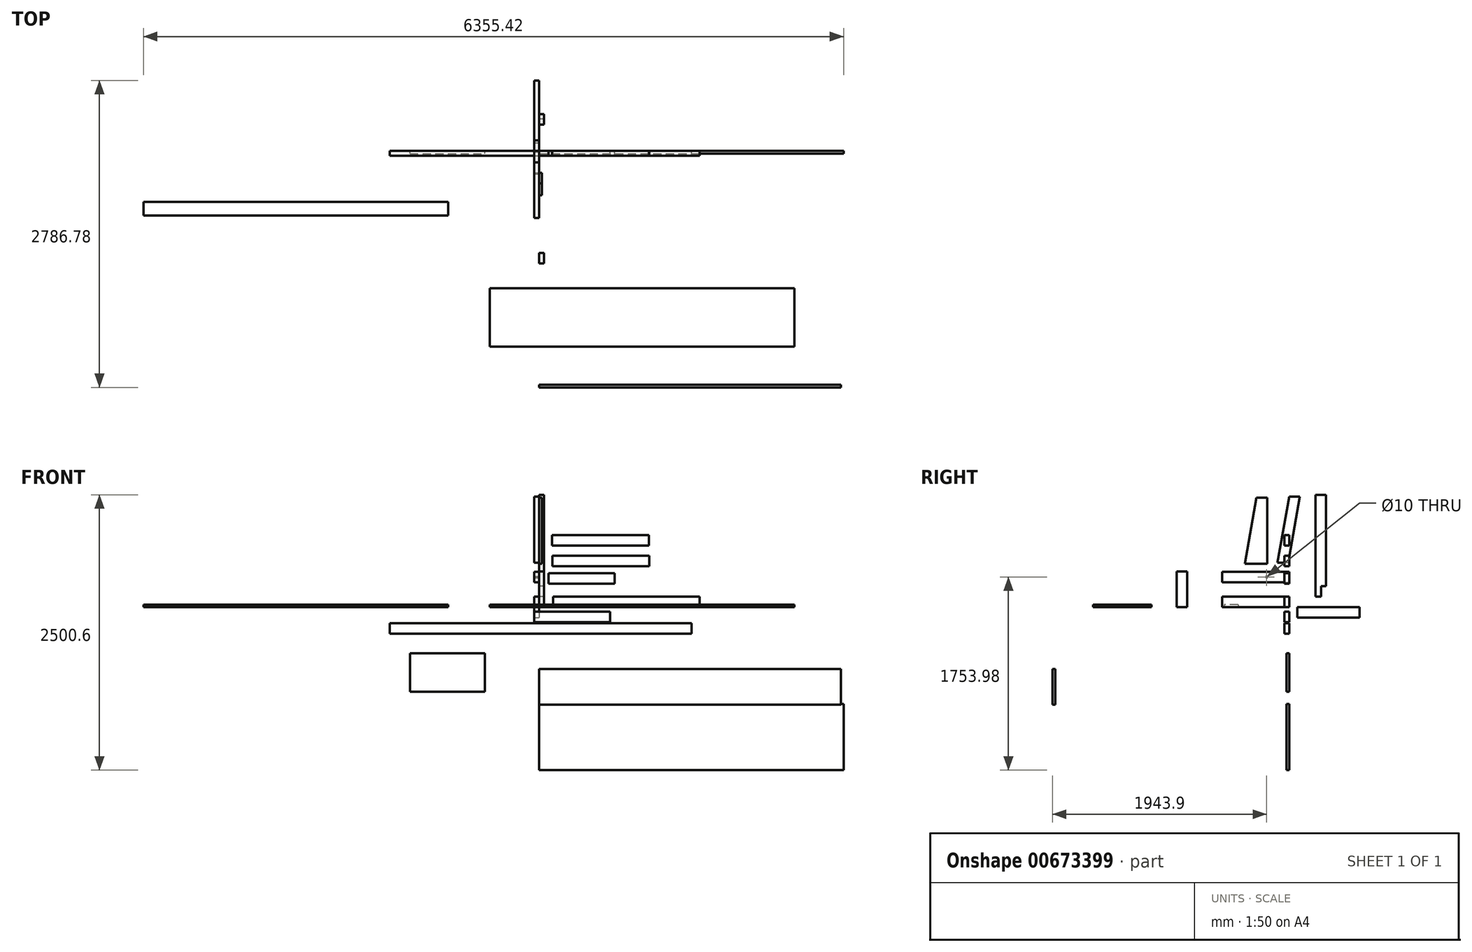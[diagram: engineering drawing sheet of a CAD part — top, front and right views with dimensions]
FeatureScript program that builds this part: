
annotation { "Feature Type Name" : "Feature", "Feature Type Description" : "" }
export const myFeature = defineFeature(function(context is Context, id is Id, definition is map)
    precondition{}
    {
        {
            var Q0;
            Q0=qCreatedBy(makeId("Right.planeOp"),FACE);
            var sketch = newSketch(context, id + "F0", { "sketchPlane" : qUnion([Q0])});
            skLineSegment(sketch, "E0", {"start": v(0, 1003.33) * mm, "end": v(-106.38, 403.33) * mm});
            skLineSegment(sketch, "E1", {"start": v(96.47, 1003.24) * mm, "end": v(-9.92, 403.24) * mm});
            skLineSegment(sketch, "E2", {"start": v(0, 1003.33) * mm, "end": v(96.47, 1003.24) * mm});
            skLineSegment(sketch, "E3", {"start": v(-9.92, 403.24) * mm, "end": v(-106.38, 403.33) * mm});
            skSolve(sketch);
        }
        {
            var Q0;
            Q0=makeQuery(id+"F0.imprint","IMPRINT",FACE,{"disambiguationData":[TD([[makeQuery(id+"F0.imprint","IMPRINT",EDGE,{"derivedFrom":sQuery(id+"F0.wireOp",EDGE,"E0")}),1.0]])]});
            extrude(context, id + "F1", {"entities" : qUnion([Q0]), "oppositeDirection" : true, "depth" : 45 * mm, "offsetDistance" : 25 * mm});
        }
        {
            var Q0;
            Q0=qCreatedBy(makeId("Right.planeOp"),FACE);
            var sketch = newSketch(context, id + "F2", { "sketchPlane" : qUnion([Q0])});
            skLineSegment(sketch, "E4.bottom", {"start": v(-610, 321.93) * mm, "end": v(0, 321.93) * mm});
            skLineSegment(sketch, "E4.top", {"start": v(-610, 226.93) * mm, "end": v(0, 226.93) * mm});
            skLineSegment(sketch, "E4.left", {"start": v(-610, 321.93) * mm, "end": v(-610, 226.93) * mm});
            skLineSegment(sketch, "E4.right", {"start": v(0, 321.93) * mm, "end": v(0, 226.93) * mm});
            skPoint(sketch, "E5.positionSnap0", {"position": v(0, 274.43) * mm});
            skCircle(sketch, "E6", {"center": v(-205, 274.43) * mm, "radius": 5 * mm});
            skSolve(sketch);
        }
        {
            var Q0;
            Q0 = qSketchRegion(id + "F2", true);
            extrude(context, id + "F3", {"entities" : qUnion([Q0]), "oppositeDirection" : true, "depth" : 45 * mm, "offsetDistance" : 25 * mm});
        }
        {
            var Q0;
            Q0=qCreatedBy(makeId("Right.planeOp"),FACE);
            var sketch = newSketch(context, id + "F4", { "sketchPlane" : qUnion([Q0])});
            skLineSegment(sketch, "E7.bottom", {"start": v(334, 1021.05) * mm, "end": v(239, 1021.05) * mm});
            skLineSegment(sketch, "E7.top", {"start": v(334, 96.05) * mm, "end": v(239, 96.05) * mm});
            skLineSegment(sketch, "E7.left", {"start": v(334, 1021.05) * mm, "end": v(334, 96.05) * mm});
            skLineSegment(sketch, "E7.right", {"start": v(239, 1021.05) * mm, "end": v(239, 96.05) * mm});
            skLineSegment(sketch, "E8.bottom", {"start": v(334, 96.05) * mm, "end": v(289, 96.05) * mm});
            skLineSegment(sketch, "E8.top", {"start": v(334, 191.05) * mm, "end": v(289, 191.05) * mm});
            skLineSegment(sketch, "E8.left", {"start": v(334, 96.05) * mm, "end": v(334, 191.05) * mm});
            skLineSegment(sketch, "E8.right", {"start": v(289, 96.05) * mm, "end": v(289, 191.05) * mm});
            skSolve(sketch);
        }
        {
            var Q0;
            Q0=makeQuery(id+"F4.imprint","IMPRINT",FACE,{"disambiguationData":[TD([[makeQuery(id+"F4.imprint","IMPRINT",EDGE,{"derivedFrom":sQuery(id+"F4.wireOp",EDGE,"E7.bottom")}),1.0]])]});
            extrude(context, id + "F5", {"entities" : qUnion([Q0]), "depth" : 45 * mm, "offsetDistance" : 25 * mm});
        }
        {
            var Q0;
            Q0=qCreatedBy(makeId("Right.planeOp"),FACE);
            var sketch = newSketch(context, id + "F6", { "sketchPlane" : qUnion([Q0])});
            skLineSegment(sketch, "E9.bottom", {"start": v(0, 0) * mm, "end": v(-610, 0) * mm});
            skLineSegment(sketch, "E9.top", {"start": v(0, 95) * mm, "end": v(-610, 95) * mm});
            skLineSegment(sketch, "E9.left", {"start": v(0, 0) * mm, "end": v(0, 95) * mm});
            skLineSegment(sketch, "E9.right", {"start": v(-610, 0) * mm, "end": v(-610, 95) * mm});
            skSolve(sketch);
        }
        {
            var Q0;
            Q0=makeQuery(id+"F6.imprint","IMPRINT",FACE,{"disambiguationData":[TD([[makeQuery(id+"F6.imprint","IMPRINT",EDGE,{"derivedFrom":sQuery(id+"F6.wireOp",EDGE,"E9.bottom")}),-1.0]])]});
            extrude(context, id + "F7", {"entities" : qUnion([Q0]), "oppositeDirection" : true, "depth" : 45 * mm, "offsetDistance" : 25 * mm});
        }
        {
            var Q0;
            Q0=qCreatedBy(makeId("Right.planeOp"),FACE);
            var sketch = newSketch(context, id + "F8", { "sketchPlane" : qUnion([Q0])});
            skLineSegment(sketch, "E10.bottom", {"start": v(-1022.82, 325) * mm, "end": v(-927.82, 325) * mm});
            skLineSegment(sketch, "E10.top", {"start": v(-1022.82, 0) * mm, "end": v(-927.82, 0) * mm});
            skLineSegment(sketch, "E10.left", {"start": v(-1022.82, 325) * mm, "end": v(-1022.82, 0) * mm});
            skLineSegment(sketch, "E10.right", {"start": v(-927.82, 325) * mm, "end": v(-927.82, 0) * mm});
            skSolve(sketch);
        }
        {
            var Q0;
            Q0=makeQuery(id+"F8.imprint","IMPRINT",FACE,{"disambiguationData":[TD([[makeQuery(id+"F8.imprint","IMPRINT",EDGE,{"derivedFrom":sQuery(id+"F8.wireOp",EDGE,"E10.bottom")}),-1.0]])]});
            extrude(context, id + "F9", {"entities" : qUnion([Q0]), "depth" : 45 * mm, "offsetDistance" : 25 * mm});
        }
        {
            var Q0;
            Q0=qCreatedBy(makeId("Front.planeOp"),FACE);
            var sketch = newSketch(context, id + "F10", { "sketchPlane" : qUnion([Q0])});
            skLineSegment(sketch, "E11.bottom", {"start": v(126.86, 0) * mm, "end": v(1456.86, 0) * mm});
            skLineSegment(sketch, "E11.top", {"start": v(126.86, 95) * mm, "end": v(1456.86, 95) * mm});
            skLineSegment(sketch, "E11.left", {"start": v(126.86, 0) * mm, "end": v(126.86, 95) * mm});
            skLineSegment(sketch, "E11.right", {"start": v(1456.86, 0) * mm, "end": v(1456.86, 95) * mm});
            skSolve(sketch);
        }
        {
            var Q0;
            Q0=makeQuery(id+"F10.imprint","IMPRINT",FACE,{"disambiguationData":[TD([[makeQuery(id+"F10.imprint","IMPRINT",EDGE,{"derivedFrom":sQuery(id+"F10.wireOp",EDGE,"E11.bottom")}),1.0]])]});
            extrude(context, id + "F11", {"entities" : qUnion([Q0]), "depth" : 45 * mm, "offsetDistance" : 25 * mm});
        }
        {
            var Q0;
            Q0=qCreatedBy(makeId("Right.planeOp"),FACE);
            var sketch = newSketch(context, id + "F12", { "sketchPlane" : qUnion([Q0])});
            skLineSegment(sketch, "E12.bottom", {"start": v(72.88, 0) * mm, "end": v(637.88, 0) * mm});
            skLineSegment(sketch, "E12.top", {"start": v(72.88, -95) * mm, "end": v(637.88, -95) * mm});
            skLineSegment(sketch, "E12.left", {"start": v(72.88, 0) * mm, "end": v(72.88, -95) * mm});
            skLineSegment(sketch, "E12.right", {"start": v(637.88, 0) * mm, "end": v(637.88, -95) * mm});
            skSolve(sketch);
        }
        {
            var Q0;
            Q0=makeQuery(id+"F12.imprint","IMPRINT",FACE,{"disambiguationData":[TD([[makeQuery(id+"F12.imprint","IMPRINT",EDGE,{"derivedFrom":sQuery(id+"F12.wireOp",EDGE,"E12.bottom")}),-1.0]])]});
            extrude(context, id + "F13", {"entities" : qUnion([Q0]), "oppositeDirection" : true, "depth" : 45 * mm, "offsetDistance" : 25 * mm});
        }
        {
            var Q0;
            Q0=qCreatedBy(makeId("Front.planeOp"),FACE);
            var sketch = newSketch(context, id + "F14", { "sketchPlane" : qUnion([Q0])});
            skLineSegment(sketch, "E13.bottom", {"start": v(87.25, 309.2) * mm, "end": v(684.75, 309.2) * mm});
            skLineSegment(sketch, "E13.top", {"start": v(87.25, 214.2) * mm, "end": v(684.75, 214.2) * mm});
            skLineSegment(sketch, "E13.left", {"start": v(87.25, 309.2) * mm, "end": v(87.25, 214.2) * mm});
            skLineSegment(sketch, "E13.right", {"start": v(684.75, 309.2) * mm, "end": v(684.75, 214.2) * mm});
            skSolve(sketch);
        }
        {
            var Q0;
            Q0 = qSketchRegion(id + "F14", true);
            extrude(context, id + "F15", {"entities" : qUnion([Q0]), "depth" : 45 * mm, "offsetDistance" : 25 * mm});
        }
        {
            var Q0;
            Q0=qCreatedBy(makeId("Front.planeOp"),FACE);
            var sketch = newSketch(context, id + "F16", { "sketchPlane" : qUnion([Q0])});
            skLineSegment(sketch, "E14.bottom", {"start": v(-43.15, -41.16) * mm, "end": v(644.35, -41.16) * mm});
            skLineSegment(sketch, "E14.top", {"start": v(-43.15, -136.16) * mm, "end": v(644.35, -136.16) * mm});
            skLineSegment(sketch, "E14.left", {"start": v(-43.15, -41.16) * mm, "end": v(-43.15, -136.16) * mm});
            skLineSegment(sketch, "E14.right", {"start": v(644.35, -41.16) * mm, "end": v(644.35, -136.16) * mm});
            skSolve(sketch);
        }
        {
            var Q0;
            Q0 = qSketchRegion(id + "F16", true);
            extrude(context, id + "F17", {"entities" : qUnion([Q0]), "depth" : 45 * mm, "offsetDistance" : 25 * mm});
        }
        {
            var Q0;
            Q0=qCreatedBy(makeId("Front.planeOp"),FACE);
            var sketch = newSketch(context, id + "F18", { "sketchPlane" : qUnion([Q0])});
            skLineSegment(sketch, "E15.bottom", {"start": v(121.17, 466.86) * mm, "end": v(1001.17, 466.86) * mm});
            skLineSegment(sketch, "E15.top", {"start": v(121.17, 371.86) * mm, "end": v(1001.17, 371.86) * mm});
            skLineSegment(sketch, "E15.left", {"start": v(121.17, 466.86) * mm, "end": v(121.17, 371.86) * mm});
            skLineSegment(sketch, "E15.right", {"start": v(1001.17, 466.86) * mm, "end": v(1001.17, 371.86) * mm});
            skSolve(sketch);
        }
        {
            var Q0;
            Q0=makeQuery(id+"F18.imprint","IMPRINT",FACE,{"disambiguationData":[TD([[makeQuery(id+"F18.imprint","IMPRINT",EDGE,{"derivedFrom":sQuery(id+"F18.wireOp",EDGE,"E15.bottom")}),-1.0]])]});
            extrude(context, id + "F19", {"entities" : qUnion([Q0]), "depth" : 45 * mm, "offsetDistance" : 25 * mm});
        }
        {
            var Q0;
            Q0=qCreatedBy(makeId("Front.planeOp"),FACE);
            var sketch = newSketch(context, id + "F20", { "sketchPlane" : qUnion([Q0])});
            skLineSegment(sketch, "E16.bottom", {"start": v(116.72, 654.45) * mm, "end": v(996.72, 654.45) * mm});
            skLineSegment(sketch, "E16.top", {"start": v(116.72, 559.45) * mm, "end": v(996.72, 559.45) * mm});
            skLineSegment(sketch, "E16.left", {"start": v(116.72, 654.45) * mm, "end": v(116.72, 559.45) * mm});
            skLineSegment(sketch, "E16.right", {"start": v(996.72, 654.45) * mm, "end": v(996.72, 559.45) * mm});
            skSolve(sketch);
        }
        {
            var Q0;
            Q0=makeQuery(id+"F20.imprint","IMPRINT",FACE,{"disambiguationData":[TD([[makeQuery(id+"F20.imprint","IMPRINT",EDGE,{"derivedFrom":sQuery(id+"F20.wireOp",EDGE,"E16.bottom")}),-1.0]])]});
            extrude(context, id + "F21", {"entities" : qUnion([Q0]), "depth" : 45 * mm, "offsetDistance" : 25 * mm});
        }
        {
            var Q0;
            Q0=qCreatedBy(makeId("Front.planeOp"),FACE);
            var sketch = newSketch(context, id + "F22", { "sketchPlane" : qUnion([Q0])});
            skLineSegment(sketch, "E17.bottom", {"start": v(-1356.74, -144.71) * mm, "end": v(1383.26, -144.71) * mm});
            skLineSegment(sketch, "E17.top", {"start": v(-1356.74, -239.71) * mm, "end": v(1383.26, -239.71) * mm});
            skLineSegment(sketch, "E17.left", {"start": v(-1356.74, -144.71) * mm, "end": v(-1356.74, -239.71) * mm});
            skLineSegment(sketch, "E17.right", {"start": v(1383.26, -144.71) * mm, "end": v(1383.26, -239.71) * mm});
            skSolve(sketch);
        }
        {
            var Q0;
            Q0=makeQuery(id+"F22.imprint","IMPRINT",FACE,{"disambiguationData":[TD([[makeQuery(id+"F22.imprint","IMPRINT",EDGE,{"derivedFrom":sQuery(id+"F22.wireOp",EDGE,"E17.bottom")}),-1.0]])]});
            extrude(context, id + "F23", {"entities" : qUnion([Q0]), "depth" : 45 * mm, "offsetDistance" : 25 * mm});
        }
        {
            var Q0;
            Q0=qCreatedBy(makeId("Front.planeOp"),FACE);
            var sketch = newSketch(context, id + "F24", { "sketchPlane" : qUnion([Q0])});
            skLineSegment(sketch, "E18.bottom", {"start": v(-1172.12, -416.8) * mm, "end": v(-492.12, -416.8) * mm});
            skLineSegment(sketch, "E18.top", {"start": v(-1172.12, -766.8) * mm, "end": v(-492.12, -766.8) * mm});
            skLineSegment(sketch, "E18.left", {"start": v(-1172.12, -416.8) * mm, "end": v(-1172.12, -766.8) * mm});
            skLineSegment(sketch, "E18.right", {"start": v(-492.12, -416.8) * mm, "end": v(-492.12, -766.8) * mm});
            skSolve(sketch);
        }
        {
            var Q0;
            Q0=makeQuery(id+"F24.imprint","IMPRINT",FACE,{"disambiguationData":[TD([[makeQuery(id+"F24.imprint","IMPRINT",EDGE,{"derivedFrom":sQuery(id+"F24.wireOp",EDGE,"E18.bottom")}),-1.0]])]});
            extrude(context, id + "F25", {"entities" : qUnion([Q0]), "depth" : 25 * mm, "offsetDistance" : 25 * mm});
        }
        {
            var Q0;
            Q0=qCreatedBy(makeId("Right.planeOp"),FACE);
            var sketch = newSketch(context, id + "F26", { "sketchPlane" : qUnion([Q0])});
            skLineSegment(sketch, "E19.bottom", {"start": v(616.1, -559.45) * mm, "end": v(-2123.9, -559.45) * mm});
            skLineSegment(sketch, "E19.top", {"start": v(616.1, -884.45) * mm, "end": v(-2123.9, -884.45) * mm});
            skLineSegment(sketch, "E19.left", {"start": v(616.1, -559.45) * mm, "end": v(616.1, -884.45) * mm});
            skLineSegment(sketch, "E19.right", {"start": v(-2123.9, -559.45) * mm, "end": v(-2123.9, -884.45) * mm});
            skSolve(sketch);
        }
        {
            var Q0;
            Q0=makeQuery(id+"F26.imprint","IMPRINT",FACE,{"disambiguationData":[TD([[makeQuery(id+"F26.imprint","IMPRINT",EDGE,{"derivedFrom":sQuery(id+"F26.wireOp",EDGE,"E19.bottom")}),1.0]])]});
            extrude(context, id + "F27", {"entities" : qUnion([Q0]), "depth" : 25 * mm, "offsetDistance" : 25 * mm});
        }
        {
            var Q0;
            Q0=makeQuery(id+"F27.opExtrude","SWEPT_BODY",BODY,{"disambiguationData":[OSD([sQuery(id+"F26.wireOp",EDGE,"E19.bottom"),sQuery(id+"F26.wireOp",EDGE,"E19.top"),sQuery(id+"F26.wireOp",EDGE,"E19.left"),sQuery(id+"F26.wireOp",EDGE,"E19.right")])]});
            var Q1;
            Q1=makeQuery(id+"F27.opExtrude","CAP_EDGE",EDGE,{"disambiguationData":[OSD([sQuery(id+"F26.wireOp",EDGE,"E19.right")])],"isStart":true});
            transform(context, id + "F28", {"entities" : qUnion([Q0]), "transformType" : TransformType.ROTATION, "transformAxis" : qUnion([Q1]), "angle" : 90 * degree, "makeCopy" : false});
        }
        {
            var Q0;
            Q0=qCreatedBy(makeId("Right.planeOp"),FACE);
            var sketch = newSketch(context, id + "F29", { "sketchPlane" : qUnion([Q0])});
            skLineSegment(sketch, "E20", {"start": v(-200.62, 995.97) * mm, "end": v(-297.09, 995.97) * mm});
            skLineSegment(sketch, "E21", {"start": v(-297.09, 995.97) * mm, "end": v(-402.89, 395.97) * mm});
            skLineSegment(sketch, "E22", {"start": v(-402.89, 395.97) * mm, "end": v(-200.62, 395.97) * mm});
            skLineSegment(sketch, "E23", {"start": v(-200.62, 395.97) * mm, "end": v(-200.62, 995.97) * mm});
            skSolve(sketch);
        }
        {
            var Q0;
            Q0=makeQuery(id+"F29.imprint","IMPRINT",FACE,{"disambiguationData":[TD([[makeQuery(id+"F29.imprint","IMPRINT",EDGE,{"derivedFrom":sQuery(id+"F29.wireOp",EDGE,"E20")}),1.0]])]});
            extrude(context, id + "F30", {"entities" : qUnion([Q0]), "depth" : 25 * mm, "offsetDistance" : 25 * mm});
        }
        {
            var Q0;
            Q0=qCreatedBy(makeId("Top.planeOp"),FACE);
            var sketch = newSketch(context, id + "F31", { "sketchPlane" : qUnion([Q0])});
            skLineSegment(sketch, "E24.bottom", {"start": v(-445.96, -1248.84) * mm, "end": v(2319.04, -1248.84) * mm});
            skLineSegment(sketch, "E24.top", {"start": v(-445.96, -1778.84) * mm, "end": v(2319.04, -1778.84) * mm});
            skLineSegment(sketch, "E24.left", {"start": v(-445.96, -1248.84) * mm, "end": v(-445.96, -1778.84) * mm});
            skLineSegment(sketch, "E24.right", {"start": v(2319.04, -1248.84) * mm, "end": v(2319.04, -1778.84) * mm});
            skSolve(sketch);
        }
        {
            var Q0;
            Q0 = qSketchRegion(id + "F31", true);
            extrude(context, id + "F32", {"entities" : qUnion([Q0]), "depth" : 25 * mm, "offsetDistance" : 25 * mm});
        }
        {
            var Q0;
            Q0=qCreatedBy(makeId("Front.planeOp"),FACE);
            var sketch = newSketch(context, id + "F33", { "sketchPlane" : qUnion([Q0])});
            skLineSegment(sketch, "E25.bottom", {"start": v(0, -879.55) * mm, "end": v(2765, -879.55) * mm});
            skLineSegment(sketch, "E25.top", {"start": v(0, -1479.55) * mm, "end": v(2765, -1479.55) * mm});
            skLineSegment(sketch, "E25.left", {"start": v(0, -879.55) * mm, "end": v(0, -1479.55) * mm});
            skLineSegment(sketch, "E25.right", {"start": v(2765, -879.55) * mm, "end": v(2765, -1479.55) * mm});
            skSolve(sketch);
        }
        {
            var Q0;
            Q0 = qSketchRegion(id + "F33", true);
            extrude(context, id + "F34", {"entities" : qUnion([Q0]), "depth" : 25 * mm, "offsetDistance" : 25 * mm});
        }
        {
            var Q0;
            Q0=qCreatedBy(makeId("Top.planeOp"),FACE);
            var sketch = newSketch(context, id + "F35", { "sketchPlane" : qUnion([Q0])});
            skLineSegment(sketch, "E26.bottom", {"start": v(-3590.42, -463.76) * mm, "end": v(-825.42, -463.76) * mm});
            skLineSegment(sketch, "E26.top", {"start": v(-3590.42, -588.76) * mm, "end": v(-825.42, -588.76) * mm});
            skLineSegment(sketch, "E26.left", {"start": v(-3590.42, -463.76) * mm, "end": v(-3590.42, -588.76) * mm});
            skLineSegment(sketch, "E26.right", {"start": v(-825.42, -463.76) * mm, "end": v(-825.42, -588.76) * mm});
            skSolve(sketch);
        }
        {
            var Q0;
            Q0=makeQuery(id+"F35.imprint","IMPRINT",FACE,{"disambiguationData":[TD([[makeQuery(id+"F35.imprint","IMPRINT",EDGE,{"derivedFrom":sQuery(id+"F35.wireOp",EDGE,"E26.bottom")}),-1.0]])]});
            extrude(context, id + "F36", {"entities" : qUnion([Q0]), "depth" : 25 * mm, "offsetDistance" : 25 * mm});
        }
    });
